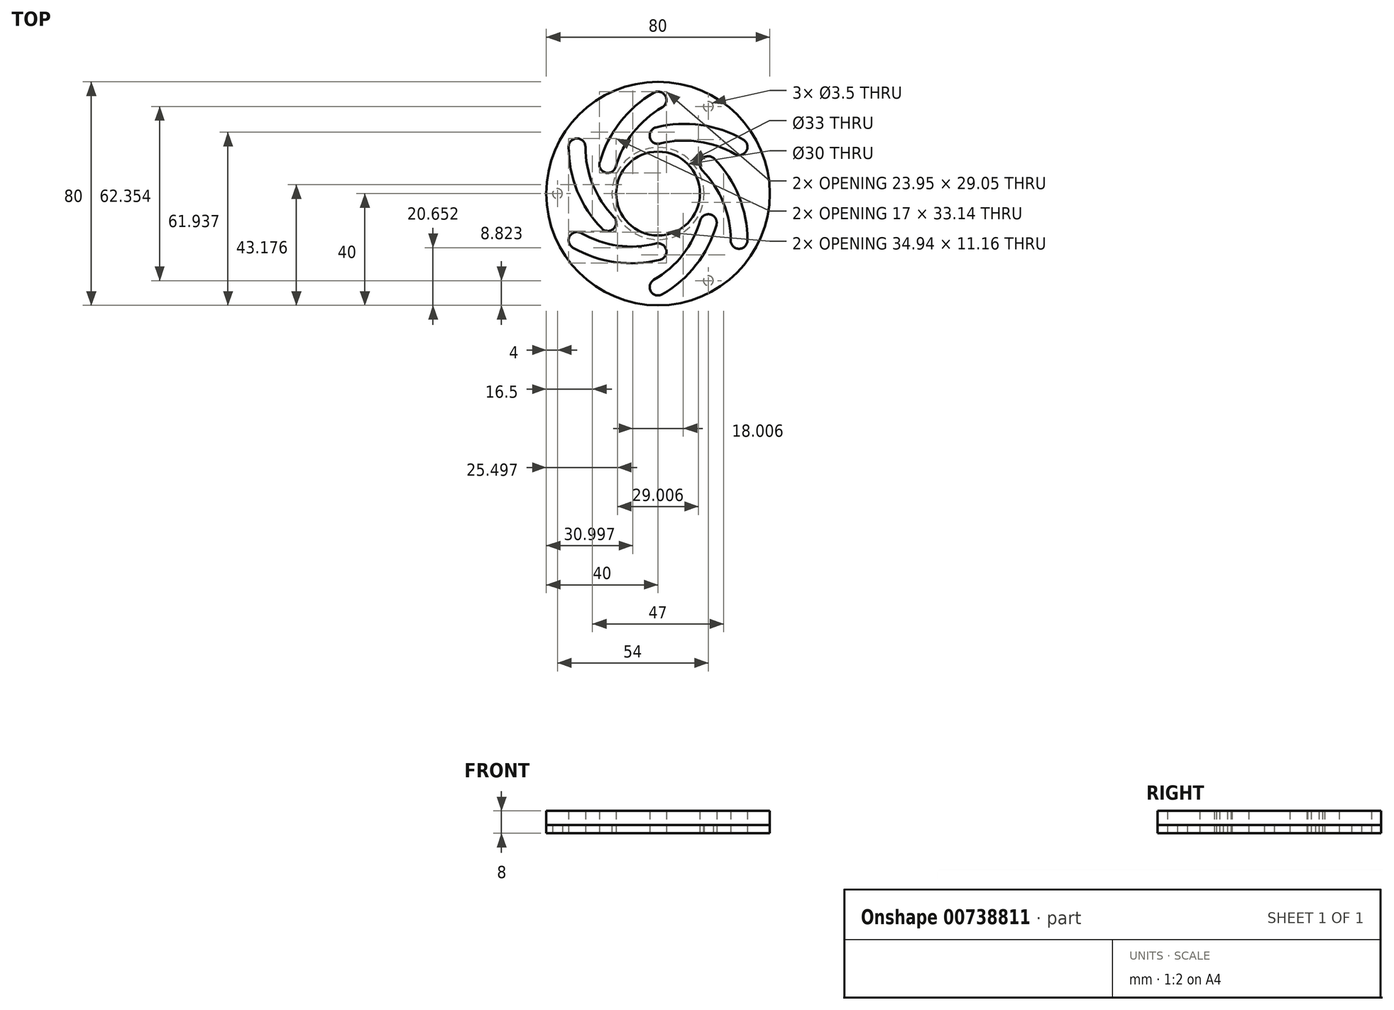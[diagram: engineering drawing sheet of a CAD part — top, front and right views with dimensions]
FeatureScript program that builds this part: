
annotation { "Feature Type Name" : "Feature", "Feature Type Description" : "" }
export const myFeature = defineFeature(function(context is Context, id is Id, definition is map)
    precondition{}
    {
        {
            var Q0;
            Q0=qCreatedBy(makeId("Top.planeOp"),FACE);
            var sketch = newSketch(context, id + "F0", { "sketchPlane" : qUnion([Q0])});
            skCircle(sketch, "E0", {"center": v(0, 0) * mm, "radius": 15 * mm});
            skCircle(sketch, "E1.0", {"center": v(0, 0) * mm, "radius": 40 * mm});
            skCircle(sketch, "E2.cCircle", {"center": v(0, 0) * mm, "radius": 18 * mm, "construction": true});
            skLineSegment(sketch, "E2.0", {"start": v(18, 10.4) * mm, "end": v(18, -10.4) * mm, "construction": true});
            skLineSegment(sketch, "E2.1", {"start": v(18, -10.4) * mm, "end": v(0, -20.78) * mm, "construction": true});
            skLineSegment(sketch, "E2.2", {"start": v(0, -20.78) * mm, "end": v(-18, -10.4) * mm, "construction": true});
            skLineSegment(sketch, "E2.3", {"start": v(-18, -10.4) * mm, "end": v(-18, 10.4) * mm, "construction": true});
            skLineSegment(sketch, "E2.4", {"start": v(-18, 10.4) * mm, "end": v(0, 20.78) * mm, "construction": true});
            skLineSegment(sketch, "E2.5", {"start": v(0, 20.78) * mm, "end": v(18, 10.4) * mm, "construction": true});
            skPoint(sketch, "E2.0.midPoint", {"position": v(18, 0) * mm});
            skCircle(sketch, "E3.cCircle", {"center": v(0, 0) * mm, "radius": 29 * mm, "construction": true});
            skLineSegment(sketch, "E3.0", {"start": v(29, 16.74) * mm, "end": v(29, -16.74) * mm, "construction": true});
            skLineSegment(sketch, "E3.1", {"start": v(29, -16.74) * mm, "end": v(0, -33.49) * mm, "construction": true});
            skLineSegment(sketch, "E3.2", {"start": v(0, -33.49) * mm, "end": v(-29, -16.74) * mm, "construction": true});
            skLineSegment(sketch, "E3.3", {"start": v(-29, -16.74) * mm, "end": v(-29, 16.74) * mm, "construction": true});
            skLineSegment(sketch, "E3.4", {"start": v(-29, 16.74) * mm, "end": v(0, 33.49) * mm, "construction": true});
            skLineSegment(sketch, "E3.5", {"start": v(0, 33.49) * mm, "end": v(29, 16.74) * mm, "construction": true});
            skPoint(sketch, "E3.0.midPoint", {"position": v(29, 0) * mm});
            skArc(sketch, "E4", {"start": v(29, 16.74) * mm, "mid": v(14.9, 21.6) * mm, "end": v(0, 20.78) * mm});
            skArc(sketch, "E5", {"start": v(0, 33.49) * mm, "mid": v(-11.25, 23.7) * mm, "end": v(-18, 10.4) * mm});
            skArc(sketch, "E6", {"start": v(-29, 16.74) * mm, "mid": v(-26.15, 2.1) * mm, "end": v(-18, -10.4) * mm});
            skArc(sketch, "E7", {"start": v(-29, -16.74) * mm, "mid": v(-14.9, -21.6) * mm, "end": v(0, -20.78) * mm});
            skArc(sketch, "E8", {"start": v(0, -33.49) * mm, "mid": v(11.25, -23.7) * mm, "end": v(18, -10.4) * mm});
            skArc(sketch, "E9", {"start": v(29, -16.74) * mm, "mid": v(26.15, -2.1) * mm, "end": v(18, 10.4) * mm});
            skArc(sketch, "E10.0.startCap", {"start": v(30.5, 19.34) * mm, "mid": v(31.6, 15.24) * mm, "end": v(27.5, 14.15) * mm});
            skArc(sketch, "E10.0.endCap", {"start": v(0.73, 17.88) * mm, "mid": v(-2.9, 20.05) * mm, "end": v(-0.73, 23.7) * mm});
            skArc(sketch, "E10.0.left", {"start": v(27.5, 14.15) * mm, "mid": v(14.48, 18.62) * mm, "end": v(0.73, 17.88) * mm});
            skArc(sketch, "E10.0.right", {"start": v(30.5, 19.34) * mm, "mid": v(15.3, 24.56) * mm, "end": v(-0.73, 23.7) * mm});
            skArc(sketch, "E10.1.startCap", {"start": v(32, -16.74) * mm, "mid": v(29, -19.74) * mm, "end": v(26, -16.74) * mm});
            skArc(sketch, "E10.1.endCap", {"start": v(15.85, 8.3) * mm, "mid": v(15.91, 12.55) * mm, "end": v(20.15, 12.48) * mm});
            skArc(sketch, "E10.1.left", {"start": v(26, -16.74) * mm, "mid": v(23.37, -3.23) * mm, "end": v(15.85, 8.3) * mm});
            skArc(sketch, "E10.1.right", {"start": v(32, -16.74) * mm, "mid": v(28.93, -0.98) * mm, "end": v(20.15, 12.48) * mm});
            skArc(sketch, "E10.2.startCap", {"start": v(1.5, -36.08) * mm, "mid": v(-2.6, -34.99) * mm, "end": v(-1.5, -30.89) * mm});
            skArc(sketch, "E10.2.endCap", {"start": v(15.11, -9.57) * mm, "mid": v(18.82, -7.5) * mm, "end": v(20.89, -11.21) * mm});
            skArc(sketch, "E10.2.left", {"start": v(-1.5, -30.89) * mm, "mid": v(8.89, -21.85) * mm, "end": v(15.11, -9.57) * mm});
            skArc(sketch, "E10.2.right", {"start": v(1.5, -36.08) * mm, "mid": v(13.62, -25.54) * mm, "end": v(20.89, -11.21) * mm});
            skArc(sketch, "E10.3.startCap", {"start": v(-30.5, -19.34) * mm, "mid": v(-31.6, -15.24) * mm, "end": v(-27.5, -14.15) * mm});
            skArc(sketch, "E10.3.endCap", {"start": v(-0.73, -17.88) * mm, "mid": v(2.9, -20.05) * mm, "end": v(0.73, -23.7) * mm});
            skArc(sketch, "E10.3.left", {"start": v(-27.5, -14.15) * mm, "mid": v(-14.48, -18.62) * mm, "end": v(-0.73, -17.88) * mm});
            skArc(sketch, "E10.3.right", {"start": v(-30.5, -19.34) * mm, "mid": v(-15.3, -24.56) * mm, "end": v(0.73, -23.7) * mm});
            skArc(sketch, "E10.4.startCap", {"start": v(-32, 16.74) * mm, "mid": v(-29, 19.74) * mm, "end": v(-26, 16.74) * mm});
            skArc(sketch, "E10.4.endCap", {"start": v(-15.85, -8.3) * mm, "mid": v(-15.91, -12.55) * mm, "end": v(-20.15, -12.48) * mm});
            skArc(sketch, "E10.4.left", {"start": v(-26, 16.74) * mm, "mid": v(-23.37, 3.23) * mm, "end": v(-15.85, -8.3) * mm});
            skArc(sketch, "E10.4.right", {"start": v(-32, 16.74) * mm, "mid": v(-28.93, 0.98) * mm, "end": v(-20.15, -12.48) * mm});
            skArc(sketch, "E10.5.startCap", {"start": v(-1.5, 36.08) * mm, "mid": v(2.6, 34.99) * mm, "end": v(1.5, 30.89) * mm});
            skArc(sketch, "E10.5.endCap", {"start": v(-15.11, 9.57) * mm, "mid": v(-18.82, 7.5) * mm, "end": v(-20.89, 11.21) * mm});
            skArc(sketch, "E10.5.left", {"start": v(1.5, 30.89) * mm, "mid": v(-8.89, 21.85) * mm, "end": v(-15.11, 9.57) * mm});
            skArc(sketch, "E10.5.right", {"start": v(-1.5, 36.08) * mm, "mid": v(-13.62, 25.54) * mm, "end": v(-20.89, 11.21) * mm});
            skSolve(sketch);
        }
        {
            var Q0;
            {var subQ0=sQuery(id+"F0.wireOp",EDGE,"E1.0");var subQ1=sQuery(id+"F0.wireOp",EDGE,"KRIlYd9P-oV2H-WIXw-96c5-SxJNxq0iZk3Y");var subQ2=makeQuery(id+"F0.imprint","INTERSECT",VERTEX,{"disambiguationData":[OD(0.0)],"derivedFrom":[subQ1,subQ0]});Q0=makeQuery(id+"F0.imprint","IMPRINT",FACE,{"disambiguationData":[TD([[makeQuery(id+"F0.imprint","IMPRINT",EDGE,{"disambiguationData":[TD([[subQ2,-1.0]])],"derivedFrom":subQ1}),-1.0]])]});}
            var Q1;
            {var subQ0=sQuery(id+"F0.wireOp",EDGE,"27e8db86-9d14-48c5-88d2-b66114e86ea9.0");var subQ1=sQuery(id+"F0.wireOp",EDGE,"E0");var subQ2=makeQuery(id+"F0.imprint","INTERSECT",VERTEX,{"disambiguationData":[OD(0.0)],"derivedFrom":[subQ1,subQ0]});Q1=makeQuery(id+"F0.imprint","IMPRINT",FACE,{"disambiguationData":[TD([[makeQuery(id+"F0.imprint","IMPRINT",EDGE,{"disambiguationData":[TD([[subQ2,1.0]])],"derivedFrom":subQ1}),-1.0]])]});}
            var Q2;
            {var subQ1=sQuery(id+"F0.wireOp",EDGE,"27e8db86-9d14-48c5-88d2-b66114e86ea9.0");var subQ3=sQuery(id+"F0.wireOp",EDGE,"E0");var subQ4=makeQuery(id+"F0.imprint","INTERSECT",VERTEX,{"disambiguationData":[OD(0.0)],"derivedFrom":[subQ3,subQ1]});Q2=makeQuery(id+"F0.imprint","IMPRINT",FACE,{"disambiguationData":[TD([[makeQuery(id+"F0.imprint","IMPRINT",EDGE,{"disambiguationData":[TD([[subQ4,-1.0]])],"derivedFrom":subQ3}),-1.0]])]});}
            var Q3;
            {var subQ0=sQuery(id+"F0.wireOp",EDGE,"E1.0");var subQ1=sQuery(id+"F0.wireOp",EDGE,"1RBqufog-SutU-u2YV-70vz-VEIsTWh3kmYH");var subQ2=makeQuery(id+"F0.imprint","INTERSECT",VERTEX,{"disambiguationData":[OD(0.0)],"derivedFrom":[subQ1,subQ0]});Q3=makeQuery(id+"F0.imprint","IMPRINT",FACE,{"disambiguationData":[TD([[makeQuery(id+"F0.imprint","IMPRINT",EDGE,{"disambiguationData":[TD([[subQ2,1.0]])],"derivedFrom":subQ1}),-1.0]])]});}
            var Q4;
            {var subQ0=sQuery(id+"F0.wireOp",EDGE,"1bafbdf1-0515-41c9-b864-16e6ee229926.0");var subQ7=sQuery(id+"F0.wireOp",EDGE,"E0");var subQ8=makeQuery(id+"F0.imprint","INTERSECT",VERTEX,{"disambiguationData":[OD(0.0)],"derivedFrom":[subQ7,subQ0]});Q4=makeQuery(id+"F0.imprint","IMPRINT",FACE,{"disambiguationData":[TD([[makeQuery(id+"F0.imprint","IMPRINT",EDGE,{"disambiguationData":[TD([[subQ8,1.0]])],"derivedFrom":subQ7}),-1.0]])]});}
            var Q5;
            {var subQ0=sQuery(id+"F0.wireOp",EDGE,"27e8db86-9d14-48c5-88d2-b66114e86ea9.0");var subQ1=sQuery(id+"F0.wireOp",EDGE,"E0");var subQ2=makeQuery(id+"F0.imprint","INTERSECT",VERTEX,{"disambiguationData":[OD(1.0)],"derivedFrom":[subQ1,subQ0]});Q5=makeQuery(id+"F0.imprint","IMPRINT",FACE,{"disambiguationData":[TD([[makeQuery(id+"F0.imprint","IMPRINT",EDGE,{"disambiguationData":[TD([[subQ2,-1.0]])],"derivedFrom":subQ1}),-1.0]])]});}
            extrude(context, id + "F1", {"entities" : qUnion([Q0, Q1, Q2, Q3, Q4, Q5]), "depth" : 8 * mm, "offsetDistance" : 25 * mm});
        }
        {
            var Q0;
            Q0=qCreatedBy(makeId("Top.planeOp"),FACE);
            var sketch = newSketch(context, id + "F2", { "sketchPlane" : qUnion([Q0])});
            skCircle(sketch, "E11", {"center": v(0, 0) * mm, "radius": 40 * mm});
            skCircle(sketch, "E12", {"center": v(0, 0) * mm, "radius": 16.5 * mm});
            skPoint(sketch, "E13.0.midPoint", {"position": v(18, 0) * mm});
            skPoint(sketch, "E14", {"position": v(-36, 0) * mm});
            skPoint(sketch, "E15", {"position": v(18, 31.18) * mm});
            skPoint(sketch, "E16", {"position": v(18, -31.18) * mm});
            skCircle(sketch, "E17", {"center": v(-36, 0) * mm, "radius": 1.75 * mm});
            skCircle(sketch, "E18", {"center": v(18, 31.18) * mm, "radius": 1.75 * mm});
            skCircle(sketch, "E19", {"center": v(18, -31.18) * mm, "radius": 1.75 * mm});
            skSolve(sketch);
        }
        {
            var Q0;
            Q0 = qSketchRegion(id + "F2", true);
            extrude(context, id + "F3", {"entities" : qUnion([Q0]), "depth" : 3 * mm, "offsetDistance" : 25 * mm});
        }
    });
